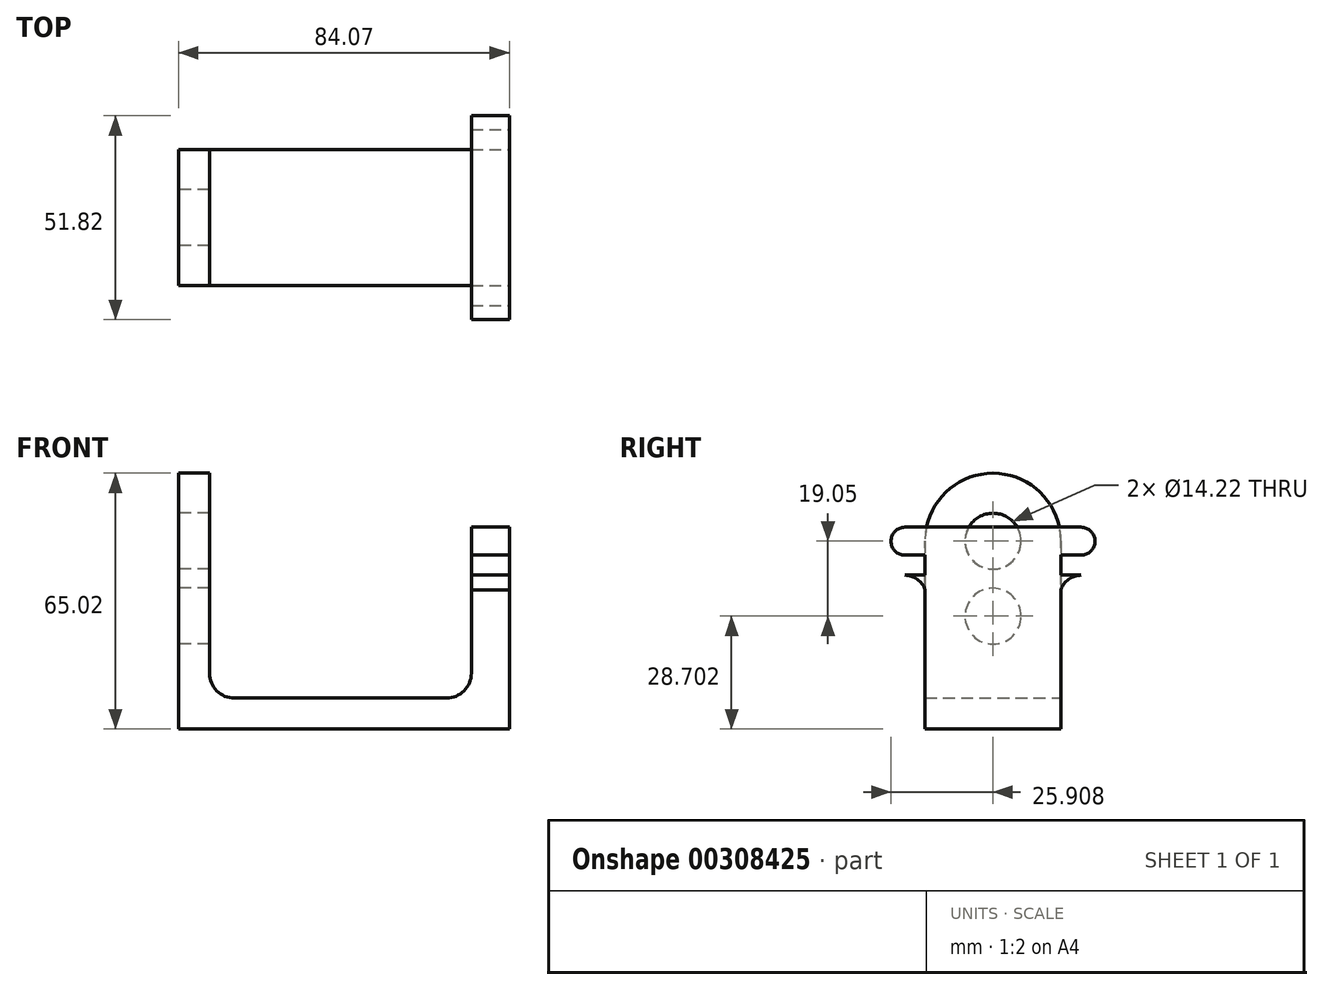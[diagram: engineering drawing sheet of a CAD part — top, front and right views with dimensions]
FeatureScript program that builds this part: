
annotation { "Feature Type Name" : "Feature", "Feature Type Description" : "" }
export const myFeature = defineFeature(function(context is Context, id is Id, definition is map)
    precondition{}
    {
        {
            var Q0;
            Q0=qCreatedBy(makeId("Front.planeOp"),FACE);
            var sketch = newSketch(context, id + "F0", { "sketchPlane" : qUnion([Q0])});
            skLineSegment(sketch, "E0", {"start": v(0, 0) * mm, "end": v(0, 47.75) * mm});
            skLineSegment(sketch, "E1", {"start": v(0, 47.75) * mm, "end": v(7.87, 47.75) * mm});
            skLineSegment(sketch, "E2", {"start": v(0, 0) * mm, "end": v(84.07, 0) * mm});
            skLineSegment(sketch, "E3", {"start": v(14.22, 7.87) * mm, "end": v(68.07, 7.87) * mm});
            skArc(sketch, "E4", {"start": v(7.87, 14.22) * mm, "mid": v(9.73, 9.73) * mm, "end": v(14.22, 7.87) * mm});
            skLineSegment(sketch, "E5", {"start": v(7.87, 47.75) * mm, "end": v(7.87, 14.22) * mm});
            skArc(sketch, "E6", {"start": v(68.07, 7.87) * mm, "mid": v(72.56, 9.73) * mm, "end": v(74.42, 14.22) * mm});
            skLineSegment(sketch, "E7", {"start": v(74.42, 14.22) * mm, "end": v(74.42, 47.75) * mm});
            skLineSegment(sketch, "E8", {"start": v(84.07, 0) * mm, "end": v(84.07, 47.75) * mm});
            skLineSegment(sketch, "E9", {"start": v(84.07, 47.75) * mm, "end": v(74.42, 47.75) * mm});
            skSolve(sketch);
        }
        {
            var Q0;
            Q0 = qSketchRegion(id + "F0", true);
            extrude(context, id + "F1", {"entities" : qUnion([Q0]), "depth" : 34.54 * mm});
        }
        {
            var Q0;
            Q0=makeQuery(id+"F1.opExtrude","SWEPT_FACE",FACE,{"disambiguationData":[OSD([sQuery(id+"F0.wireOp",EDGE,"E8")])]});
            var sketch = newSketch(context, id + "F2", { "sketchPlane" : qUnion([Q0])});
            skLineSegment(sketch, "E10", {"start": v(-17.27, 0) * mm, "end": v(-17.27, 47.75) * mm, "construction": true});
            skLineSegment(sketch, "E11", {"start": v(-39.62, 47.75) * mm, "end": v(5.08, 47.75) * mm, "construction": true});
            skArc(sketch, "E12.0.startCap", {"start": v(-39.62, 44.2) * mm, "mid": v(-43.18, 47.75) * mm, "end": v(-39.62, 51.3) * mm});
            skArc(sketch, "E12.0.endCap", {"start": v(5.08, 51.3) * mm, "mid": v(8.64, 47.75) * mm, "end": v(5.08, 44.2) * mm});
            skLineSegment(sketch, "E12.0.left", {"start": v(-39.62, 51.3) * mm, "end": v(5.08, 51.3) * mm});
            skLineSegment(sketch, "E12.0.right", {"start": v(-39.62, 44.2) * mm, "end": v(5.08, 44.2) * mm});
            skArc(sketch, "E13.0.startCap", {"start": v(-39.62, 39.12) * mm, "mid": v(-48.26, 47.75) * mm, "end": v(-39.62, 56.39) * mm});
            skArc(sketch, "E13.0.endCap", {"start": v(5.08, 56.39) * mm, "mid": v(13.72, 47.75) * mm, "end": v(5.08, 39.12) * mm});
            skLineSegment(sketch, "E13.0.left", {"start": v(-39.62, 56.39) * mm, "end": v(5.08, 56.39) * mm});
            skLineSegment(sketch, "E13.0.right", {"start": v(-39.62, 39.12) * mm, "end": v(5.08, 39.12) * mm});
            skArc(sketch, "E14", {"start": v(-34.54, 35.4) * mm, "mid": v(-36.48, 38.1) * mm, "end": v(-39.62, 39.12) * mm});
            skArc(sketch, "E15", {"start": v(5.08, 39.12) * mm, "mid": v(1.94, 38.1) * mm, "end": v(0, 35.4) * mm});
            skLineSegment(sketch, "E16", {"start": v(0, 35.4) * mm, "end": v(0, 39.12) * mm});
            skLineSegment(sketch, "E17", {"start": v(-34.54, 35.4) * mm, "end": v(-34.54, 39.12) * mm});
            skLineSegment(sketch, "E18", {"start": v(0, 47.75) * mm, "end": v(0, 44.2) * mm});
            skLineSegment(sketch, "E19", {"start": v(0, 47.75) * mm, "end": v(-34.54, 47.75) * mm});
            skLineSegment(sketch, "E20", {"start": v(-34.54, 47.75) * mm, "end": v(-34.54, 44.2) * mm});
            skLineSegment(sketch, "E21", {"start": v(-34.54, 47.75) * mm, "end": v(-34.54, 39.12) * mm});
            skLineSegment(sketch, "E22", {"start": v(-34.54, 47.75) * mm, "end": v(0, 47.75) * mm});
            skLineSegment(sketch, "E23", {"start": v(0, 39.12) * mm, "end": v(0, 47.75) * mm});
            skSolve(sketch);
        }
        {
            var Q0;
            {var subQ5=sQuery(id+"F2.wireOp",EDGE,"E22");Q0=makeQuery(id+"F2.imprint","IMPRINT",FACE,{"disambiguationData":[TD([[makeQuery(id+"F2.imprint","IMPRINT",EDGE,{"derivedFrom":subQ5}),-1.0]])]});}
            var Q1;
            {var subQ0=sQuery(id+"F2.wireOp",EDGE,"E21");var subQ1=sQuery(id+"F2.wireOp",EDGE,"E12.0.right");var subQ2=makeQuery(id+"F2.imprint","INTERSECT",VERTEX,{"derivedFrom":[subQ1,subQ0]});Q1=makeQuery(id+"F2.imprint","IMPRINT",FACE,{"disambiguationData":[TD([[makeQuery(id+"F2.imprint","IMPRINT",EDGE,{"disambiguationData":[TD([[subQ2,-1.0]])],"derivedFrom":subQ1}),-1.0]])]});}
            extrude(context, id + "F3", {"entities" : qUnion([Q0, Q1]), "operationType" : NewBodyOperationType.REMOVE, "oppositeDirection" : true, "depth" : 9.65 * mm});
        }
        {
            var Q0;
            {var subQ0=sQuery(id+"F2.wireOp",EDGE,"E21");var subQ1=sQuery(id+"F2.wireOp",EDGE,"E12.0.right");var subQ2=makeQuery(id+"F2.imprint","INTERSECT",VERTEX,{"derivedFrom":[subQ1,subQ0]});Q0=makeQuery(id+"F2.imprint","IMPRINT",FACE,{"disambiguationData":[TD([[makeQuery(id+"F2.imprint","IMPRINT",EDGE,{"disambiguationData":[TD([[subQ2,-1.0]])],"derivedFrom":subQ1}),-1.0]])]});}
            var Q1;
            {var subQ10=sQuery(id+"F2.wireOp",EDGE,"E12.0.startCap");Q1=makeQuery(id+"F2.imprint","IMPRINT",FACE,{"disambiguationData":[TD([[makeQuery(id+"F2.imprint","IMPRINT",EDGE,{"derivedFrom":subQ10}),1.0]])]});}
            var Q2;
            {var subQ0=sQuery(id+"F2.wireOp",EDGE,"E14");Q2=makeQuery(id+"F2.imprint","IMPRINT",FACE,{"disambiguationData":[TD([[makeQuery(id+"F2.imprint","IMPRINT",EDGE,{"derivedFrom":subQ0}),-1.0]])]});}
            var Q3;
            {var subQ0=sQuery(id+"F2.wireOp",EDGE,"E15");Q3=makeQuery(id+"F2.imprint","IMPRINT",FACE,{"disambiguationData":[TD([[makeQuery(id+"F2.imprint","IMPRINT",EDGE,{"derivedFrom":subQ0}),-1.0]])]});}
            extrude(context, id + "F4", {"entities" : qUnion([Q0, Q1, Q2, Q3]), "operationType" : NewBodyOperationType.ADD, "oppositeDirection" : true, "depth" : 9.65 * mm});
        }
        {
            var Q0;
            Q0=makeQuery(id+"F1.opExtrude","SWEPT_FACE",FACE,{"disambiguationData":[OSD([sQuery(id+"F0.wireOp",EDGE,"E0")])]});
            var sketch = newSketch(context, id + "F5", { "sketchPlane" : qUnion([Q0])});
            skArc(sketch, "E24", {"start": v(34.54, 47.75) * mm, "mid": v(17.27, 65.02) * mm, "end": v(0, 47.75) * mm});
            skCircle(sketch, "E25", {"center": v(17.27, 47.75) * mm, "radius": 7.11 * mm});
            skCircle(sketch, "E26", {"center": v(17.27, 28.7) * mm, "radius": 7.11 * mm});
            skSolve(sketch);
        }
        {
            var Q0;
            {var subQ0=sQuery(id+"F5.wireOp",EDGE,"E24");Q0=makeQuery(id+"F5.imprint","IMPRINT",FACE,{"disambiguationData":[TD([[makeQuery(id+"F5.imprint","IMPRINT",EDGE,{"derivedFrom":subQ0}),1.0]])]});}
            extrude(context, id + "F6", {"entities" : qUnion([Q0]), "operationType" : NewBodyOperationType.ADD, "oppositeDirection" : true, "depth" : 7.87 * mm});
        }
        {
            var Q0;
            Q0 = qSketchRegion(id + "F5", true);
            extrude(context, id + "F7", {"entities" : qUnion([Q0]), "operationType" : NewBodyOperationType.REMOVE, "oppositeDirection" : true, "depth" : 7.87 * mm});
        }
    });
